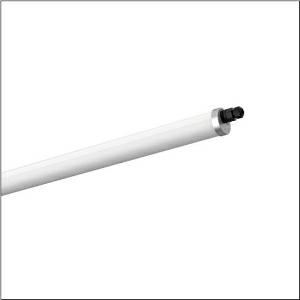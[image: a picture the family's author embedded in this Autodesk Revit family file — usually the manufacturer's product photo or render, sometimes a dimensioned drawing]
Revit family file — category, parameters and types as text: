
# Revit family: monsun_r__31_tube_51ft107n460a_2b58
name_source: partatom
category: Lighting Fixtures
units: mm (PartAtom-declared; Revit-internal decimal feet)

## family parameters
Cut with Voids When Loaded = No
Host = Face
Light Source = No
Part Type = Normal
Room Calculation Point = No
Round Connector Dimension = Use Diameter
Shared = No

## types (1)
- Monsun® 31 Tube (1 x LED, 6500 lm, 40 W, 4000K)
    Apparent Load = 40 VA
    CIE Flux Codes = 42 71 90 91 100
    Color Rendering = 80
    Color Temperature = 4000K
    Default Elevation = 1800 mm
    Description = Monsun® 31 Tube, tubular luminaire, primary optical cover: diffuser, of PMMA, light emission: direct distribution, primary light characteristic: symmetric, installation type: suspended mounting, surface-mounted, LED, rated luminous flux: 6.500lm, luminous efficacy: 160lm/W, light colour: 840, colour temperature: 4000K, control gear: ON/OFF, with with 1 terminal, 3-pole, max. 2.5mm², through-wiring: 3x 1.5mm², mains connection: 220..240V, AC, 50/60Hz, rated input power: 40W, housing, cylindrical, of PMMA, semi-transparent, matt white, with luminaire and ceiling fastening, V4A, mounting with brackets of stainless steel, length: 1.560mm, diameter: 75mm, end cap, of stainless steel (V4A), protection rating (complete): IP67/IP69K, insulation class (complete): insulation class I (protective earthing), certification: CE, UKCA, impact resistance: IK07, permissible operating ambient temperature: -20..+40°C, corresponds to IFS (International Featured Standards) requirements for safety and quality in the food industry, usage in unprotected outdoor areas possible with horizontal mounting, contact your sales advisor before using the luminaires in applications with unclear chemical exposure, large temperature fluctuations or condensation-forming humidity, packaging unit: 1 piece
    Height = 83 mm
    Lamp = 1 x LED
    Lamp Light Flux = 6500 lm
    Lamp Power = 40 W
    Lamp count = 1
    Length = 1560 mm
    Luminous efficacy = 163 lm/W
    Manufacturer = Siteco
    ModVariant = No
    Model = 51FT107N460A
    Mounting Place = Ceiling
    Mounting Type = Pendant
    Number of Poles = 1
    OnlyDefault = Yes
    Power Factor = 1
    Product Name = Monsun® 31 Tube
    Product group = tubular luminaire
    ProductGroupID = 906
    Protection Class = Protection class I
    RLX_Detail_Level = 1
    RLX_Emergency_Light_Flux = 0 lm
    RLX_Emergency_Type = 0
    RLX_Emergency_Type_DB = No
    RlxData = <blob elided: 25277 chars, md5=a9d5c362>
    Socket = socket
    Standby Power = 0 W
    System Light Flux = 6500 lm
    System Power = 40 W
    Type Comments = Product without accessories
    Type Image = l_1228461.jpg
    URL = http://relux.com
    VarID = ---
    Voltage = 0 V
    Weight = 0.00 kg
    Width = 75 mm

## geometry (parser evidence)
native form markers: Blend x4, Sweep x16
no freeform markers — native parametric forms only
